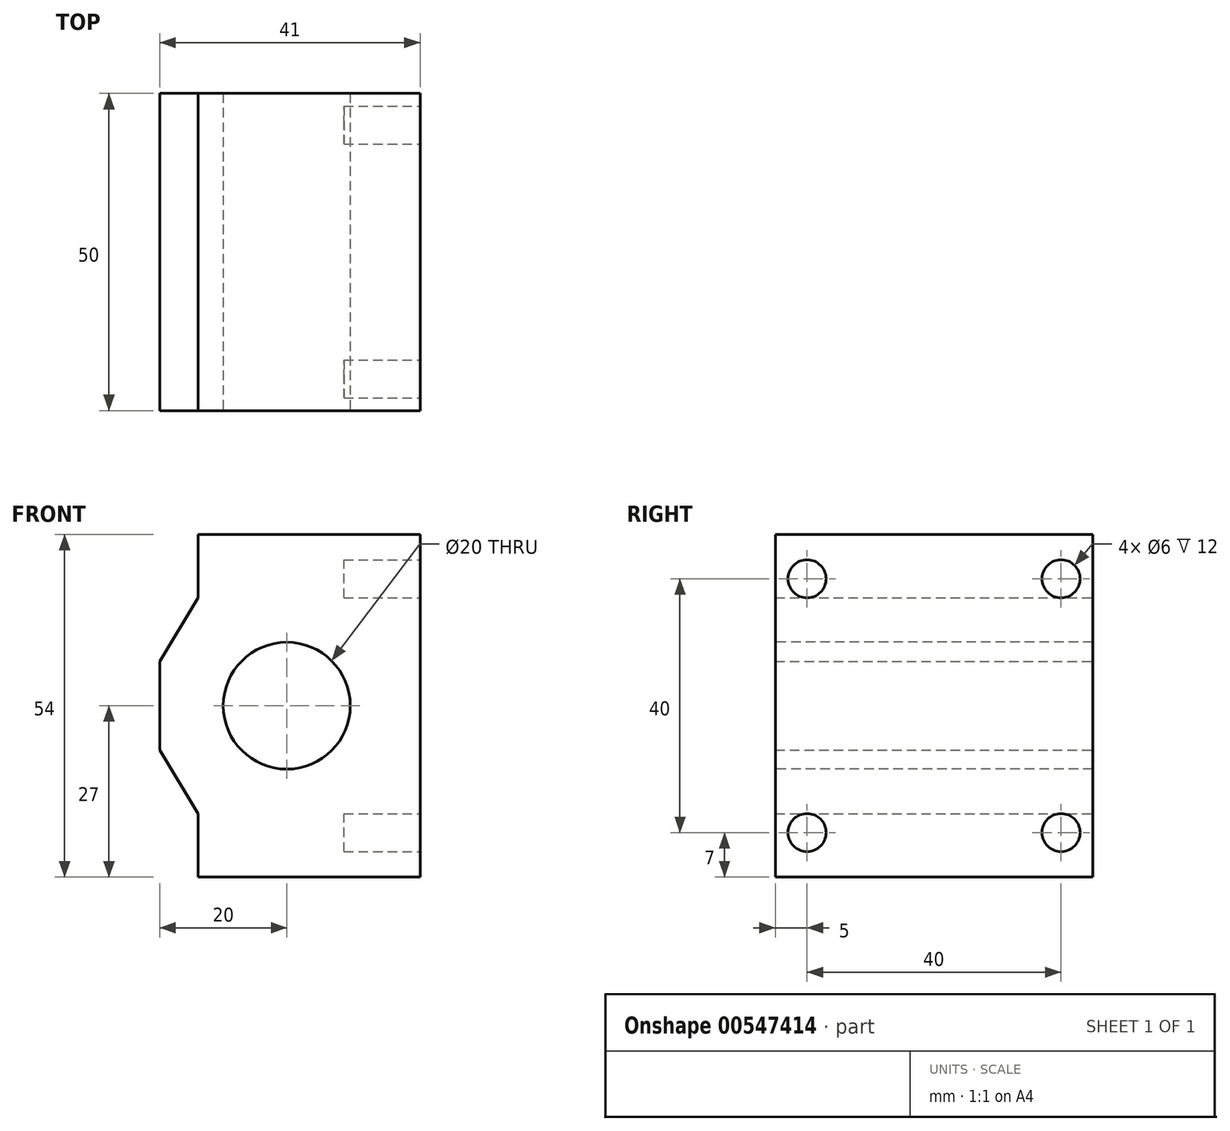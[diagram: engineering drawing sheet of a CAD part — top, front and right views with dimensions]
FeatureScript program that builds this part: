
annotation { "Feature Type Name" : "Feature", "Feature Type Description" : "" }
export const myFeature = defineFeature(function(context is Context, id is Id, definition is map)
    precondition{}
    {
        {
            var Q0;
            Q0=qCreatedBy(makeId("Front.planeOp"),FACE);
            var sketch = newSketch(context, id + "F0", { "sketchPlane" : qUnion([Q0])});
            skLineSegment(sketch, "E0.bottom", {"start": v(20.5, 27) * mm, "end": v(-14.5, 27) * mm});
            skLineSegment(sketch, "E0.top", {"start": v(20.5, -27) * mm, "end": v(-14.5, -27) * mm});
            skLineSegment(sketch, "E0.left", {"start": v(20.5, 27) * mm, "end": v(20.5, -27) * mm});
            skLineSegment(sketch, "E0.right", {"start": v(-20.5, 7) * mm, "end": v(-20.5, -7) * mm});
            skPoint(sketch, "E0.middle", {"position": v(0, 0) * mm});
            skLineSegment(sketch, "E1", {"start": v(-14.5, 27) * mm, "end": v(-14.5, 17) * mm});
            skLineSegment(sketch, "E2", {"start": v(-14.5, 17) * mm, "end": v(-20.5, 7) * mm});
            skLineSegment(sketch, "E3", {"start": v(-14.5, -27) * mm, "end": v(-14.5, -17) * mm});
            skLineSegment(sketch, "E4", {"start": v(-14.5, -17) * mm, "end": v(-20.5, -7) * mm});
            skPoint(sketch, "E5.orphan", {"position": v(-20.5, -27) * mm});
            skPoint(sketch, "E6.orphan", {"position": v(-20.5, 27) * mm});
            skSolve(sketch);
        }
        {
            var Q0;
            Q0 = qSketchRegion(id + "F0", true);
            extrude(context, id + "F1", {"entities" : qUnion([Q0]), "endBound" : BoundingType.SYMMETRIC, "depth" : 50 * mm, "offsetDistance" : 25 * mm});
        }
        {
            var Q0;
            Q0=makeQuery(id+"F1.opExtrude","CAP_FACE",FACE,{"disambiguationData":[OSD([sQuery(id+"F0.wireOp",EDGE,"E0.bottom"),sQuery(id+"F0.wireOp",EDGE,"E0.top"),sQuery(id+"F0.wireOp",EDGE,"E0.left"),sQuery(id+"F0.wireOp",EDGE,"E0.right"),sQuery(id+"F0.wireOp",EDGE,"E1"),sQuery(id+"F0.wireOp",EDGE,"E2"),sQuery(id+"F0.wireOp",EDGE,"E3"),sQuery(id+"F0.wireOp",EDGE,"E4")])],"isStart":false});
            var sketch = newSketch(context, id + "F2", { "sketchPlane" : qUnion([Q0])});
            skCircle(sketch, "E7", {"center": v(-0.5, 0) * mm, "radius": 10 * mm});
            skSolve(sketch);
        }
        {
            var Q0;
            Q0 = qSketchRegion(id + "F2", true);
            extrude(context, id + "F3", {"entities" : qUnion([Q0]), "operationType" : NewBodyOperationType.REMOVE, "oppositeDirection" : true, "depth" : 50 * mm, "offsetDistance" : 25 * mm});
        }
        {
            var Q0;
            Q0=makeQuery(id+"F1.opExtrude","SWEPT_FACE",FACE,{"disambiguationData":[OSD([sQuery(id+"F0.wireOp",EDGE,"E0.left")])]});
            var sketch = newSketch(context, id + "F4", { "sketchPlane" : qUnion([Q0])});
            skCircle(sketch, "E8", {"center": v(-20, 20) * mm, "radius": 3 * mm});
            skCircle(sketch, "E9", {"center": v(20, 20) * mm, "radius": 3 * mm});
            skCircle(sketch, "E10", {"center": v(20, -20) * mm, "radius": 3 * mm});
            skCircle(sketch, "E11", {"center": v(-20, -20) * mm, "radius": 3 * mm});
            skSolve(sketch);
        }
        {
            var Q0;
            Q0 = qSketchRegion(id + "F4", true);
            extrude(context, id + "F5", {"entities" : qUnion([Q0]), "operationType" : NewBodyOperationType.REMOVE, "oppositeDirection" : true, "depth" : 12 * mm, "offsetDistance" : 25 * mm});
        }
    });
